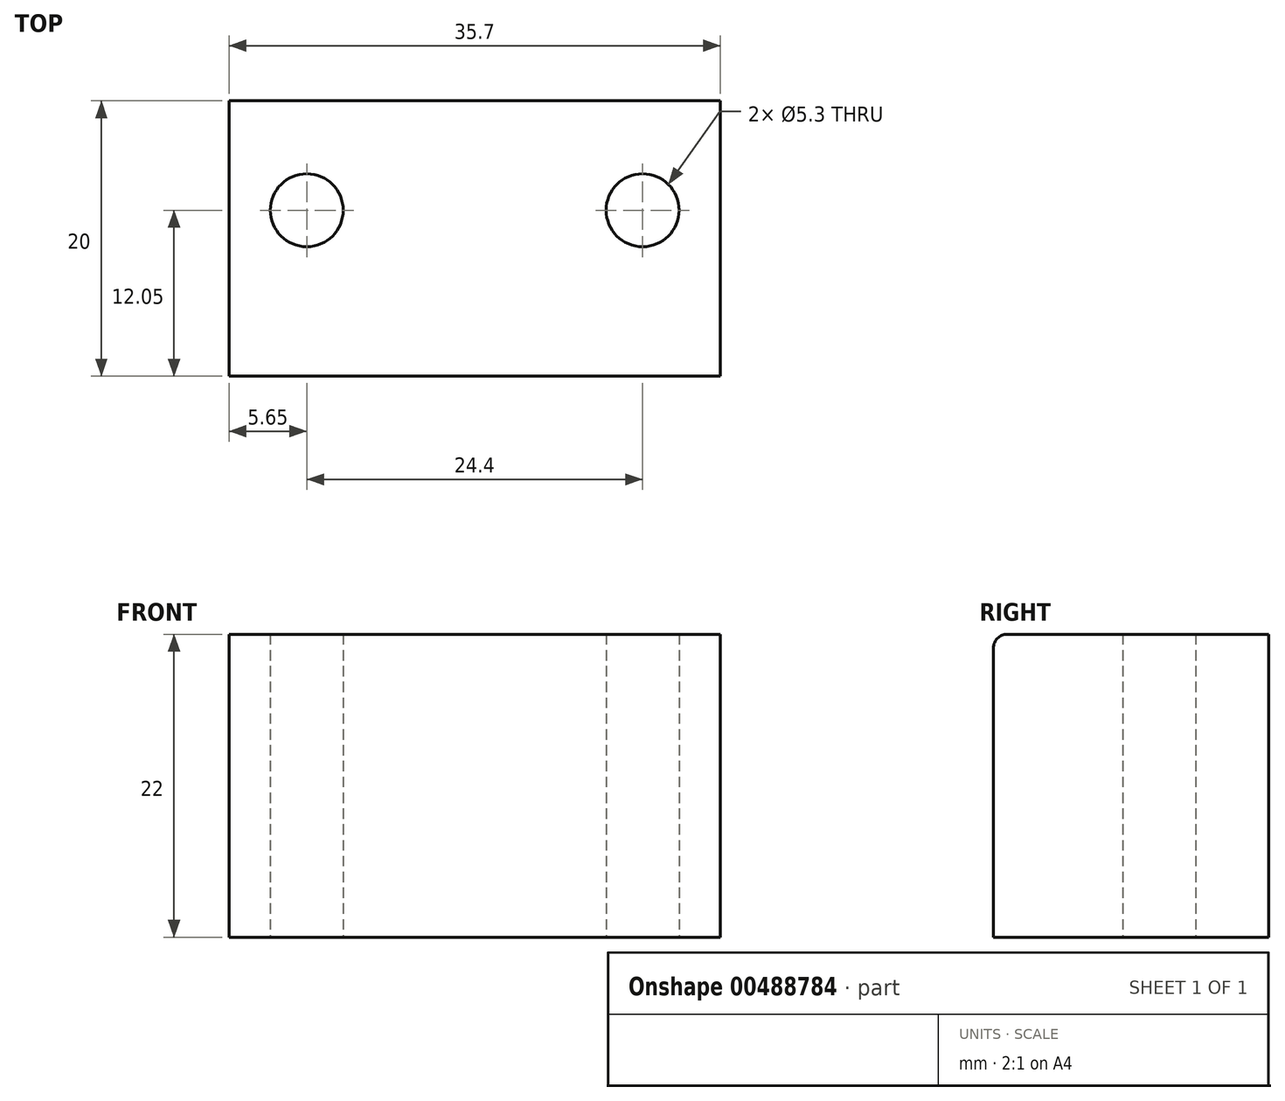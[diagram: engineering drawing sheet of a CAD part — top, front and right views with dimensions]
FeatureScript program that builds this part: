
annotation { "Feature Type Name" : "Feature", "Feature Type Description" : "" }
export const myFeature = defineFeature(function(context is Context, id is Id, definition is map)
    precondition{}
    {
        {
            var Q0;
            Q0=qCreatedBy(makeId("Top.planeOp"),FACE);
            var sketch = newSketch(context, id + "F0", { "sketchPlane" : qUnion([Q0])});
            skLineSegment(sketch, "E0.bottom", {"start": v(17.85, 10) * mm, "end": v(-17.85, 10) * mm});
            skLineSegment(sketch, "E0.top", {"start": v(17.85, -10) * mm, "end": v(-17.85, -10) * mm});
            skLineSegment(sketch, "E0.left", {"start": v(17.85, 10) * mm, "end": v(17.85, -10) * mm});
            skLineSegment(sketch, "E0.right", {"start": v(-17.85, 10) * mm, "end": v(-17.85, -10) * mm});
            skPoint(sketch, "E0.middle", {"position": v(0, 0) * mm});
            skCircle(sketch, "E1", {"center": v(-12.2, 2.05) * mm, "radius": 2.65 * mm});
            skCircle(sketch, "E2", {"center": v(12.2, 2.05) * mm, "radius": 2.65 * mm});
            skSolve(sketch);
        }
        {
            var Q0;
            Q0=makeQuery(id+"F0.imprint","IMPRINT",FACE,{"disambiguationData":[TD([[makeQuery(id+"F0.imprint","IMPRINT",EDGE,{"derivedFrom":sQuery(id+"F0.wireOp",EDGE,"E0.bottom")}),1.0]])]});
            extrude(context, id + "F1", {"entities" : qUnion([Q0]), "depth" : 22 * mm});
        }
        {
            var Q0;
            Q0=makeQuery(id+"F1.opExtrude","CAP_EDGE",EDGE,{"disambiguationData":[OSD([sQuery(id+"F0.wireOp",EDGE,"E0.top")])],"isStart":false});
            fillet(context, id + "F2", {"entities" : qUnion([Q0]), "radius" : 1 * mm, "tangentPropagation" : true, "allowEdgeOverflow" : false});
        }
    });
